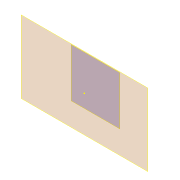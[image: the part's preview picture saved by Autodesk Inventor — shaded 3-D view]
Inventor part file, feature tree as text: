
AUTODESK INVENTOR PART (.ipt)
format: ipt  version: 2022 (Build 260153000, 153)  size: 64,000 bytes
history: native  units: mm
features: plane x2, other x2, sketch x1
ambient origin geometry x8: Origin, YZ Plane, XZ Plane, XY Plane, X Axis, Y Axis, Z Axis, Center Point
feature tree (5):
  plane  "Arbeitsebene1"
  plane  "Arbeitsebene2"
  sketch  "Skizze1"
  other  "Baugruppe5"
  other  "IM_Matchboxscope_base:1"
